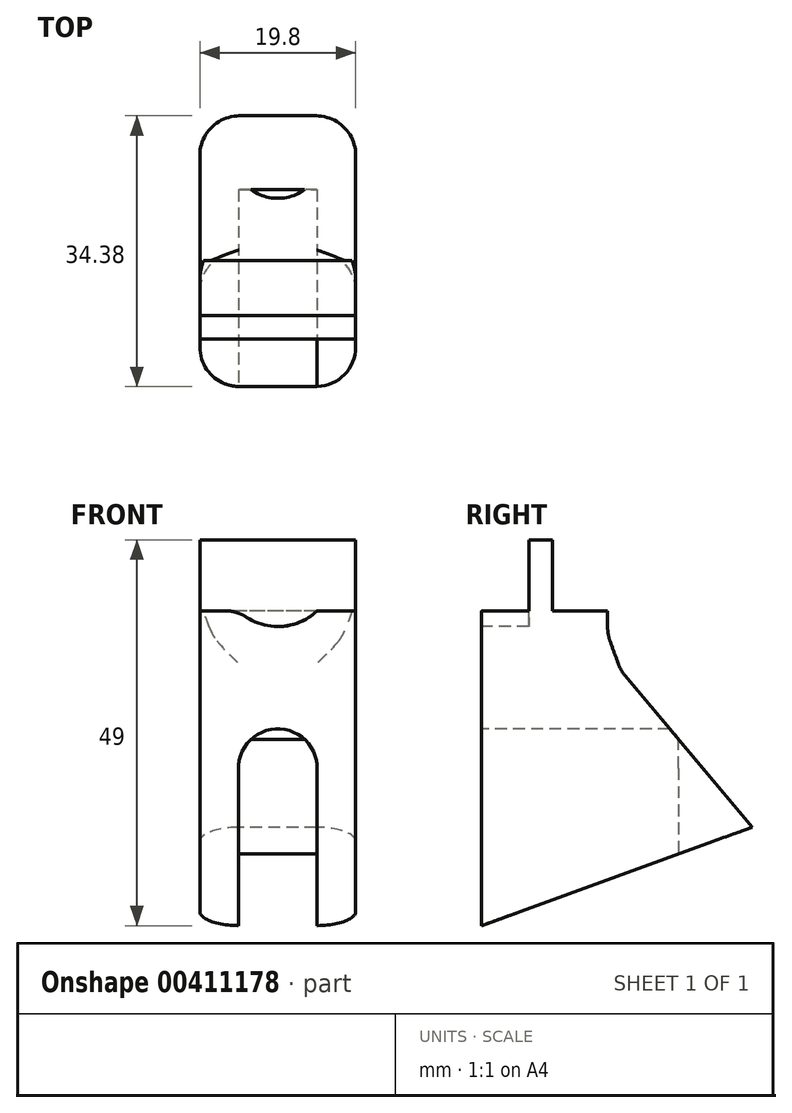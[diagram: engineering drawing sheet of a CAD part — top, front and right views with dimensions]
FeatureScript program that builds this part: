
annotation { "Feature Type Name" : "Feature", "Feature Type Description" : "" }
export const myFeature = defineFeature(function(context is Context, id is Id, definition is map)
    precondition{}
    {
        {
            var Q0;
            Q0=qCreatedBy(makeId("Right.planeOp"),FACE);
            var sketch = newSketch(context, id + "F0", { "sketchPlane" : qUnion([Q0])});
            skLineSegment(sketch, "E0.bottom", {"start": v(0, 0) * mm, "end": v(3, 0) * mm});
            skLineSegment(sketch, "E0.top", {"start": v(0, 9) * mm, "end": v(3, 9) * mm});
            skLineSegment(sketch, "E0.left", {"start": v(0, 0) * mm, "end": v(0, 9) * mm});
            skLineSegment(sketch, "E0.right", {"start": v(3, 0) * mm, "end": v(3, 9) * mm});
            skLineSegment(sketch, "E1.bottom", {"start": v(0, 0) * mm, "end": v(10, 0) * mm});
            skLineSegment(sketch, "E1.top", {"start": v(0, -3) * mm, "end": v(10, -3) * mm});
            skLineSegment(sketch, "E1.left", {"start": v(0, 0) * mm, "end": v(0, -3) * mm});
            skLineSegment(sketch, "E1.right", {"start": v(10, 0) * mm, "end": v(10, -3) * mm});
            skLineSegment(sketch, "E2.bottom", {"start": v(10, 0) * mm, "end": v(7.2, 0) * mm});
            skLineSegment(sketch, "E2.top", {"start": v(10, 9) * mm, "end": v(7.2, 9) * mm});
            skLineSegment(sketch, "E2.left", {"start": v(10, 0) * mm, "end": v(10, 9) * mm});
            skLineSegment(sketch, "E2.right", {"start": v(7.2, 0) * mm, "end": v(7.2, 9) * mm});
            skLineSegment(sketch, "E3", {"start": v(0, 0) * mm, "end": v(-6, 0) * mm});
            skLineSegment(sketch, "E4", {"start": v(-6, 0) * mm, "end": v(-6, -40) * mm});
            skLineSegment(sketch, "E5", {"start": v(-6, -40) * mm, "end": v(20.02, -30.53) * mm});
            skLineSegment(sketch, "E6", {"start": v(20.02, -30.53) * mm, "end": v(10, -3) * mm});
            skLineSegment(sketch, "E7", {"start": v(0, -3) * mm, "end": v(11.19, -33.74) * mm, "construction": true});
            skLineSegment(sketch, "E8.MirrorCS", {"start": v(2.67, 3.15) * mm, "end": v(28.38, -27.49) * mm});
            skLineSegment(sketch, "E9", {"start": v(20.02, -30.53) * mm, "end": v(28.38, -27.49) * mm});
            skSolve(sketch);
        }
        {
            var Q0;
            Q0=makeQuery(id+"F0.imprint","IMPRINT",FACE,{"disambiguationData":[TD([[makeQuery(id+"F0.imprint","IMPRINT",EDGE,{"derivedFrom":sQuery(id+"F0.wireOp",EDGE,"E0.top")}),-1.0]])]});
            var Q1;
            Q1=makeQuery(id+"F0.imprint","IMPRINT",FACE,{"disambiguationData":[TD([[makeQuery(id+"F0.imprint","IMPRINT",EDGE,{"derivedFrom":sQuery(id+"F0.wireOp",EDGE,"E2.bottom")}),-1.0]])]});
            var Q2;
            Q2=makeQuery(id+"F0.imprint","IMPRINT",FACE,{"disambiguationData":[TD([[makeQuery(id+"F0.imprint","IMPRINT",EDGE,{"derivedFrom":sQuery(id+"F0.wireOp",EDGE,"E1.top")}),1.0]])]});
            var Q3;
            Q3=makeQuery(id+"F0.imprint","IMPRINT",FACE,{"disambiguationData":[TD([[makeQuery(id+"F0.imprint","IMPRINT",EDGE,{"derivedFrom":sQuery(id+"F0.wireOp",EDGE,"E1.top")}),-1.0]])]});
            var Q4;
            {var subQ0=sQuery(id+"F0.wireOp",EDGE,"E9");Q4=makeQuery(id+"F0.imprint","IMPRINT",FACE,{"disambiguationData":[TD([[makeQuery(id+"F0.imprint","IMPRINT",EDGE,{"derivedFrom":subQ0}),1.0]])]});}
            var Q5;
            {var subQ0=sQuery(id+"F0.wireOp",EDGE,"E1.left");Q5=makeQuery(id+"F0.imprint","IMPRINT",FACE,{"disambiguationData":[TD([[makeQuery(id+"F0.imprint","IMPRINT",EDGE,{"derivedFrom":subQ0}),-1.0]])]});}
            extrude(context, id + "F1", {"entities" : qUnion([Q0, Q1, Q2, Q3, Q4, Q5]), "depth" : 19.8 * mm});
        }
        {
            var Q0;
            Q0=makeQuery(id+"F1.opExtrude","SWEPT_FACE",FACE,{"disambiguationData":[OSD([sQuery(id+"F0.wireOp",EDGE,"E4")])]});
            var sketch = newSketch(context, id + "F2", { "sketchPlane" : qUnion([Q0])});
            skLineSegment(sketch, "E10", {"start": v(9.9, -40) * mm, "end": v(9.9, 0) * mm, "construction": true});
            skCircle(sketch, "E11", {"center": v(9.9, -20) * mm, "radius": 5 * mm});
            skLineSegment(sketch, "E12", {"start": v(14.9, -20) * mm, "end": v(14.9, -40) * mm});
            skLineSegment(sketch, "E13.MirrorCS", {"start": v(4.9, -20) * mm, "end": v(4.9, -40) * mm});
            skLineSegment(sketch, "E14", {"start": v(4.9, -20) * mm, "end": v(4.9, 0) * mm, "construction": true});
            skLineSegment(sketch, "E15.MirrorCS", {"start": v(14.9, -20) * mm, "end": v(14.9, 0) * mm, "construction": true});
            skArc(sketch, "E16", {"start": v(4.9, 0) * mm, "mid": v(9.9, -2) * mm, "end": v(14.9, 0) * mm});
            skSolve(sketch);
        }
        {
            var Q0;
            Q0=makeQuery(id+"F1.opExtrude","CAP_EDGE",EDGE,{"disambiguationData":[OSD([sQuery(id+"F0.wireOp",EDGE,"E4")])],"isStart":true});
            var Q1;
            Q1=makeQuery(id+"F1.opExtrude","CAP_EDGE",EDGE,{"disambiguationData":[OSD([sQuery(id+"F0.wireOp",EDGE,"E4")])],"isStart":false});
            var Q2;
            Q2=makeQuery(id+"F1.opExtrude","CAP_EDGE",EDGE,{"disambiguationData":[OSD([sQuery(id+"F0.wireOp",EDGE,"E8.MirrorCS")])],"isStart":false});
            var Q3;
            Q3=makeQuery(id+"F1.opExtrude","CAP_EDGE",EDGE,{"disambiguationData":[OSD([sQuery(id+"F0.wireOp",EDGE,"E8.MirrorCS")])],"isStart":true});
            var Q4;
            Q4=makeQuery(id+"F1.opExtrude","SWEPT_EDGE",EDGE,{"disambiguationData":[OSD([sQuery(id+"F0.wireOp",EDGE,"E1.top"),sQuery(id+"F0.wireOp",EDGE,"E1.right"),sQuery(id+"F0.wireOp",EDGE,"E6")])]});
            var Q5;
            Q5=makeQuery(id+"F1.opExtrude","SWEPT_EDGE",EDGE,{"disambiguationData":[OSD([sQuery(id+"F0.wireOp",EDGE,"E6"),sQuery(id+"F0.wireOp",EDGE,"E8.MirrorCS")])]});
            fillet(context, id + "F3", {"entities" : qUnion([Q0, Q1, Q2, Q3, Q4, Q5]), "radius" : 5 * mm, "tangentPropagation" : true, "allowEdgeOverflow" : false});
        }
        {
            var Q0;
            {var subQ0=sQuery(id+"F2.wireOp",EDGE,"E16");Q0=makeQuery(id+"F2.imprint","IMPRINT",FACE,{"disambiguationData":[TD([[makeQuery(id+"F2.imprint","IMPRINT",EDGE,{"derivedFrom":subQ0}),1.0]])]});}
            var Q1;
            Q1=makeQuery(id+"F1.opExtrude","SWEPT_FACE",FACE,{"disambiguationData":[OSD([sQuery(id+"F0.wireOp",EDGE,"E0.left")])]});
            extrude(context, id + "F4", {"entities" : qUnion([Q0]), "operationType" : NewBodyOperationType.REMOVE, "endBound" : BoundingType.UP_TO_SURFACE, "oppositeDirection" : true, "endBoundEntityFace" : qUnion([Q1]), "depth" : 25 * mm});
        }
        {
            var Q0;
            {var subQ0=sQuery(id+"F2.wireOp",EDGE,"E16");var subQ1=sQuery(id+"F0.wireOp",EDGE,"E4");var subQ2=sQuery(id+"F0.wireOp",EDGE,"E3");Q0=makeQuery(id+"F4.boolean.opBoolean","COPY",EDGE,{"derivedFrom":makeQuery(id+"F4.opExtrude","SWEPT_EDGE",EDGE,{"disambiguationData":[OSD([subQ2,subQ1,subQ0]),TDD([makeQuery(id+"F2.imprint","INTERSECT",VERTEX,{"disambiguationData":[OD(0.0)],"derivedFrom":[makeQuery(id+"F1.opExtrude","SWEPT_EDGE",EDGE,{"disambiguationData":[OSD([subQ2,subQ1])]}),subQ0]})])]})});}
            var Q1;
            {var subQ0=sQuery(id+"F2.wireOp",EDGE,"E16");var subQ1=sQuery(id+"F0.wireOp",EDGE,"E4");var subQ2=sQuery(id+"F0.wireOp",EDGE,"E3");Q1=makeQuery(id+"F4.boolean.opBoolean","COPY",EDGE,{"derivedFrom":makeQuery(id+"F4.opExtrude","SWEPT_EDGE",EDGE,{"disambiguationData":[OSD([subQ2,subQ1,subQ0]),TDD([makeQuery(id+"F2.imprint","INTERSECT",VERTEX,{"disambiguationData":[OD(1.0)],"derivedFrom":[makeQuery(id+"F1.opExtrude","SWEPT_EDGE",EDGE,{"disambiguationData":[OSD([subQ2,subQ1])]}),subQ0]})])]})});}
            fillet(context, id + "F5", {"entities" : qUnion([Q0, Q1]), "radius" : 5 * mm, "tangentPropagation" : true, "allowEdgeOverflow" : false});
        }
        {
            var Q0;
            {var subQ0=sQuery(id+"F2.wireOp",EDGE,"E11");var subQ1=makeQuery(id+"F2.imprint","INTERSECT",VERTEX,{"derivedFrom":[subQ0,sQuery(id+"F2.wireOp",EDGE,"E12")]});Q0=makeQuery(id+"F2.imprint","IMPRINT",FACE,{"disambiguationData":[TD([[makeQuery(id+"F2.imprint","IMPRINT",EDGE,{"disambiguationData":[TD([[subQ1,-1.0]])],"derivedFrom":subQ0}),1.0]])]});}
            var Q1;
            {var subQ0=sQuery(id+"F2.wireOp",EDGE,"E12");Q1=makeQuery(id+"F2.imprint","IMPRINT",FACE,{"disambiguationData":[TD([[makeQuery(id+"F2.imprint","IMPRINT",EDGE,{"derivedFrom":subQ0}),-1.0]])]});}
            extrude(context, id + "F6", {"entities" : qUnion([Q0, Q1]), "operationType" : NewBodyOperationType.REMOVE, "oppositeDirection" : true, "depth" : 25 * mm});
        }
    });
